# Revit family: cb88820d-ad17-4b8a-bff6-943289d5a41e
name_source: partatom
category: Plumbing Fixtures
revit_build: Autodesk Revit 2014 (Build: 20130308_1515(x64)
units: mm (PartAtom-declared; Revit-internal decimal feet)

## types (1)
- cb88820d-ad17-4b8a-bff6-943289d5a41e
    Assembly Code = D2010400
    Default Elevation = 0' - 0"
    Expected Lifespan (Years) = 0
    Fixture Finish = Finish - TOTO - Cotton 01
    Keynote = 22 40 00
    Maintenance Schedule (Months) = 0
    Manufacturer = TOTO USA
    Manufacturer Fax = 770-282-8697
    Manufacturer Website = http://www.totousa.com
    Model = As Specified
    Product Data = http://www.arcat.com
    Revision = R1_2016-12
    Sales Information = http://www.totousa.com
    Standards Conformance = as Specified
    URL = http://www.totousa.com
    Unit Depth = 1' - 5 5/8"
    Unit Height = 0' - 2"
    Unit Width = 2' - 5 3/8"
    Warranty Duration (Years) = 0

## geometry (parser evidence)
native form markers: Sweep x3
no freeform markers — native parametric forms only
